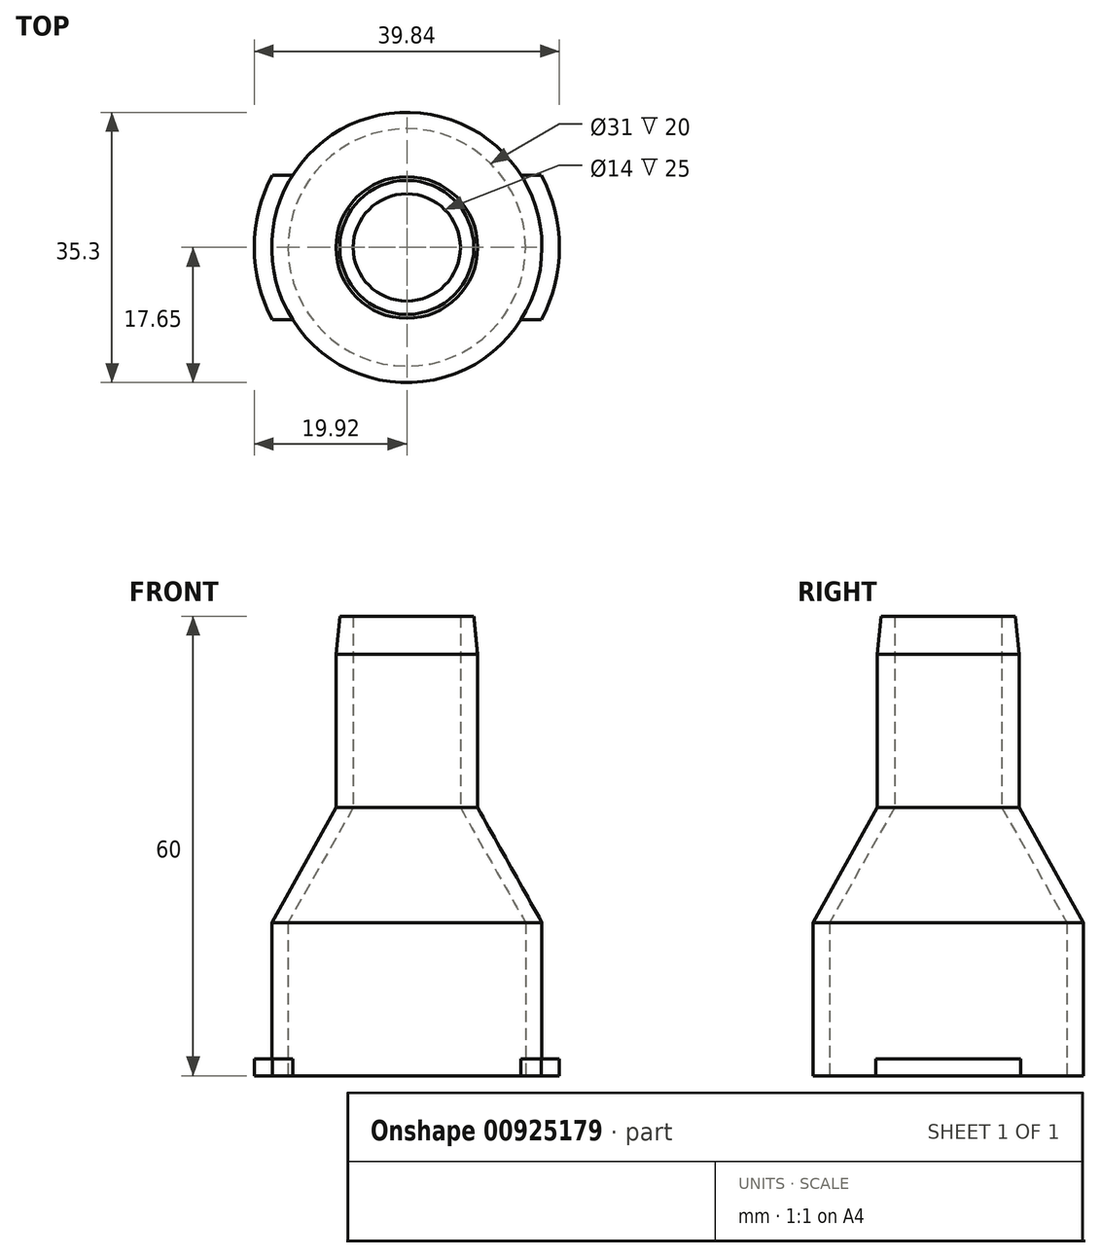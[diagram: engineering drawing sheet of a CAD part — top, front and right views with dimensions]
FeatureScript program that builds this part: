
annotation { "Feature Type Name" : "Feature", "Feature Type Description" : "" }
export const myFeature = defineFeature(function(context is Context, id is Id, definition is map)
    precondition{}
    {
        {
            var Q0;
            Q0=qCreatedBy(makeId("Top.planeOp"),FACE);
            var sketch = newSketch(context, id + "F0", { "sketchPlane" : qUnion([Q0])});
            skCircle(sketch, "E0", {"center": v(0, 0) * mm, "radius": 17.65 * mm});
            skCircle(sketch, "E1", {"center": v(0, 0) * mm, "radius": 15.5 * mm});
            skArc(sketch, "E2", {"start": v(-17.54, 9.45) * mm, "mid": v(-19.93, 0) * mm, "end": v(-17.54, -9.45) * mm});
            skLineSegment(sketch, "E3.bottom", {"start": v(17.54, -9.45) * mm, "end": v(-17.54, -9.45) * mm});
            skLineSegment(sketch, "E3.top", {"start": v(17.54, 9.45) * mm, "end": v(-17.54, 9.45) * mm});
            skArc(sketch, "E4.trimOffspring", {"start": v(17.54, -9.45) * mm, "mid": v(19.93, 0) * mm, "end": v(17.54, 9.45) * mm});
            skSolve(sketch);
        }
        {
            var Q0;
            Q0=makeQuery(id+"F0.imprint","IMPRINT",FACE,{"disambiguationData":[TD([[makeQuery(id+"F0.imprint","IMPRINT",EDGE,{"derivedFrom":sQuery(id+"F0.wireOp",EDGE,"E0")}),-1.0]])]});
            var Q1;
            Q1=makeQuery(id+"F0.imprint","IMPRINT",FACE,{"disambiguationData":[TD([[makeQuery(id+"F0.imprint","IMPRINT",EDGE,{"derivedFrom":sQuery(id+"F0.wireOp",EDGE,"E0")}),1.0]])]});
            extrude(context, id + "F1", {"entities" : qUnion([Q0, Q1]), "depth" : 2.2 * mm, "offsetDistance" : 25 * mm});
        }
        {
            var Q0;
            Q0=makeQuery(id+"F0.imprint","IMPRINT",FACE,{"disambiguationData":[TD([[makeQuery(id+"F0.imprint","IMPRINT",EDGE,{"derivedFrom":sQuery(id+"F0.wireOp",EDGE,"E0")}),1.0]])]});
            extrude(context, id + "F2", {"entities" : qUnion([Q0]), "operationType" : NewBodyOperationType.ADD, "depth" : 20 * mm, "offsetDistance" : 25 * mm});
        }
        {
            var Q0;
            Q0=makeQuery(id+"F2.opExtrude","CAP_FACE",FACE,{"disambiguationData":[OSD([sQuery(id+"F0.wireOp",EDGE,"E0"),sQuery(id+"F0.wireOp",EDGE,"E1")])],"isStart":false});
            cPlane(context, id + "F3", {"entities" : qUnion([Q0]), "cplaneType" : CPlaneType.OFFSET, "offset" : 15 * mm, "width" : 150 * mm, "height" : 150 * mm});
        }
        {
            var Q0;
            Q0=qCreatedBy(id+"F3.planeOp",FACE);
            var sketch = newSketch(context, id + "F4", { "sketchPlane" : qUnion([Q0])});
            skCircle(sketch, "E5", {"center": v(0, 0) * mm, "radius": 9.25 * mm});
            skCircle(sketch, "E6", {"center": v(0, 0) * mm, "radius": 7 * mm});
            skSolve(sketch);
        }
        {
            var Q0;
            Q0=makeQuery(id+"F4.imprint","IMPRINT",FACE,{"disambiguationData":[TD([[makeQuery(id+"F4.imprint","IMPRINT",EDGE,{"derivedFrom":sQuery(id+"F4.wireOp",EDGE,"E5")}),1.0]])]});
            extrude(context, id + "F5", {"entities" : qUnion([Q0]), "depth" : 25 * mm, "offsetDistance" : 25 * mm});
        }
        {
            var Q0;
            Q0=qCreatedBy(makeId("Right.planeOp"),FACE);
            var sketch = newSketch(context, id + "F6", { "sketchPlane" : qUnion([Q0])});
            skLineSegment(sketch, "E7", {"start": v(-17.65, 20) * mm, "end": v(-9.25, 35) * mm});
            skLineSegment(sketch, "E8", {"start": v(-9.25, 35) * mm, "end": v(-7, 35) * mm});
            skLineSegment(sketch, "E9", {"start": v(-7, 35) * mm, "end": v(-15.5, 20) * mm});
            skLineSegment(sketch, "E10", {"start": v(-15.5, 20) * mm, "end": v(-17.65, 20) * mm});
            skLineSegment(sketch, "E11", {"start": v(0, 46.74) * mm, "end": v(0, -9.03) * mm, "construction": true});
            skSolve(sketch);
        }
        {
            var Q0;
            Q0=makeQuery(id+"F6.imprint","IMPRINT",FACE,{"disambiguationData":[TD([[makeQuery(id+"F6.imprint","IMPRINT",EDGE,{"derivedFrom":sQuery(id+"F6.wireOp",EDGE,"E7")}),-1.0]])]});
            var Q1;
            Q1=sQuery(id+"F6.wireOp",EDGE,"E11");
            revolve(context, id + "F7", {"operationType" : NewBodyOperationType.ADD, "surfaceOperationType" : NewSurfaceOperationType.NEW, "entities" : qUnion([Q0]), "axis" : qUnion([Q1]), "revolveType" : RevolveType.FULL});
        }
        {
            var Q0;
            Q0=makeQuery(id+"F5.opExtrude","CAP_EDGE",EDGE,{"disambiguationData":[OSD([sQuery(id+"F4.wireOp",EDGE,"E5")])],"isStart":false});
            chamfer(context, id + "F8", {"entities" : qUnion([Q0]), "chamferType" : ChamferType.TWO_OFFSETS, "width1" : 0.5 * mm, "oppositeDirection" : false, "width2" : 5 * mm, "tangentPropagation" : true});
        }
    });
